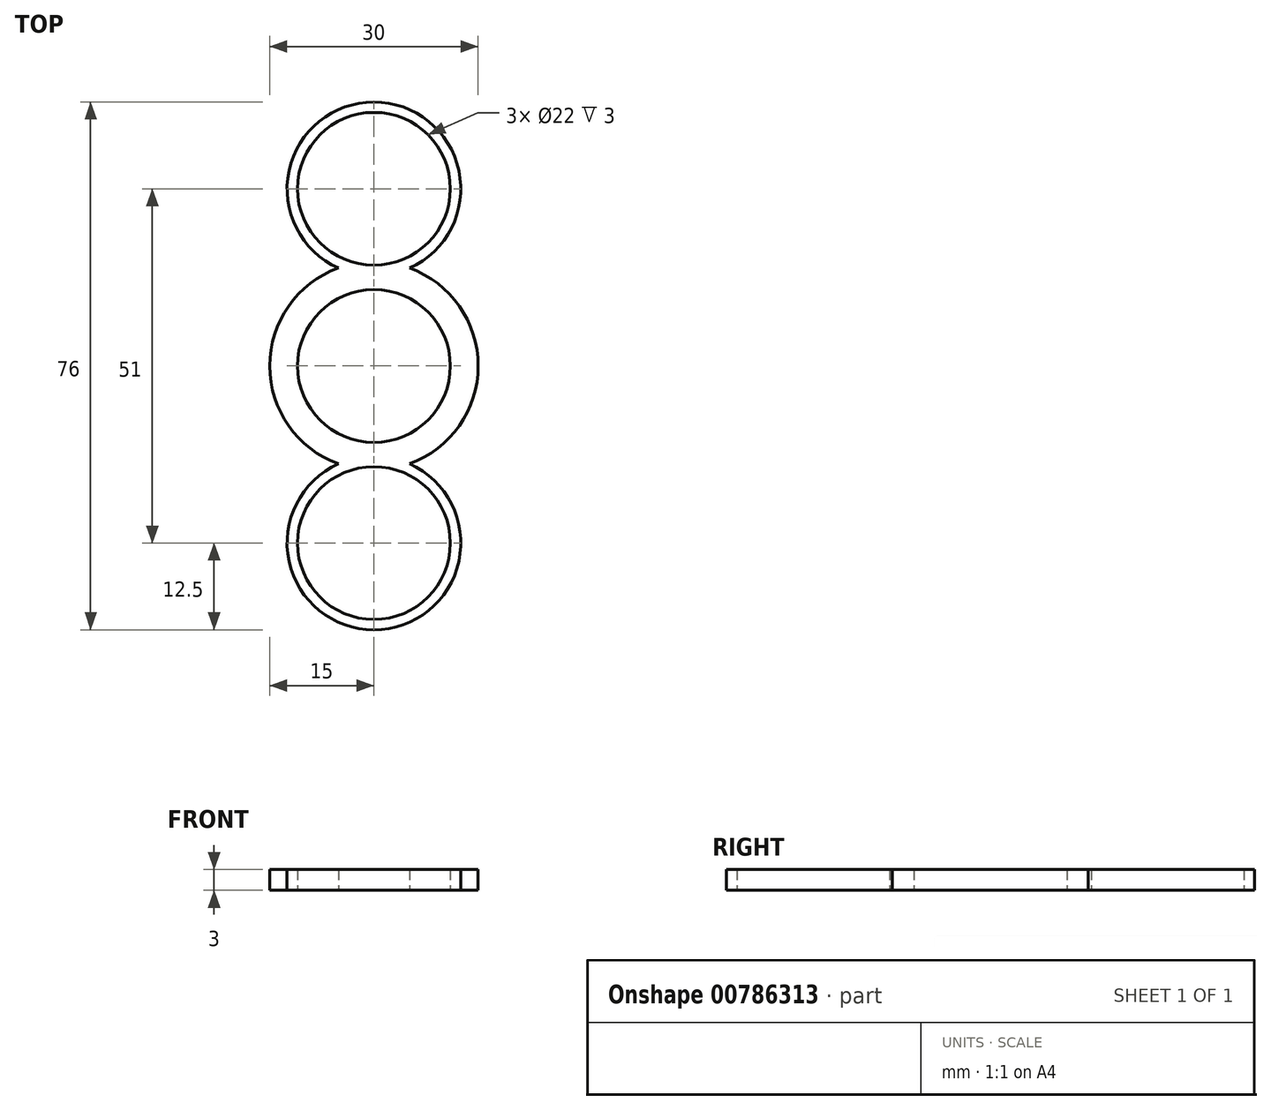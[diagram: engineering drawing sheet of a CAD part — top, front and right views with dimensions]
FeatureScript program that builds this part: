
annotation { "Feature Type Name" : "Feature", "Feature Type Description" : "" }
export const myFeature = defineFeature(function(context is Context, id is Id, definition is map)
    precondition{}
    {
        {
            var Q0;
            Q0=qCreatedBy(makeId("Top.planeOp"),FACE);
            var sketch = newSketch(context, id + "F0", { "sketchPlane" : qUnion([Q0])});
            skArc(sketch, "E0", {"start": v(11, 0) * mm, "mid": v(0, 11) * mm, "end": v(-11, 0) * mm});
            skArc(sketch, "E1", {"start": v(-5.12, 14.1) * mm, "mid": v(-12.29, 8.6) * mm, "end": v(-15, 0) * mm});
            skCircle(sketch, "E2", {"center": v(0, 25.5) * mm, "radius": 11 * mm});
            skArc(sketch, "E3", {"start": v(5.12, 14.1) * mm, "mid": v(0, 38) * mm, "end": v(-5.12, 14.1) * mm});
            skArc(sketch, "E4.trimOffspring", {"start": v(15, 0) * mm, "mid": v(12.29, 8.6) * mm, "end": v(5.12, 14.1) * mm});
            skPoint(sketch, "E5.start.orphan", {"position": v(-26.18, 0) * mm});
            skArc(sketch, "E6.1.0", {"start": v(-5.12, -14.1) * mm, "mid": v(0, -38) * mm, "end": v(5.12, -14.1) * mm});
            skCircle(sketch, "E6.1.1", {"center": v(0, -25.5) * mm, "radius": 11 * mm});
            skArc(sketch, "E6.1.2", {"start": v(-15, 0) * mm, "mid": v(-12.29, -8.6) * mm, "end": v(-5.12, -14.1) * mm});
            skArc(sketch, "E6.1.3", {"start": v(-11, 0) * mm, "mid": v(0, -11) * mm, "end": v(11, 0) * mm});
            skArc(sketch, "E6.1.4", {"start": v(5.12, -14.1) * mm, "mid": v(12.29, -8.6) * mm, "end": v(15, 0) * mm});
            skSolve(sketch);
        }
        {
            var Q0;
            Q0 = qSketchRegion(id + "F0", true);
            extrude(context, id + "F1", {"entities" : qUnion([Q0]), "depth" : 3 * mm, "offsetDistance" : 25 * mm});
        }
    });
